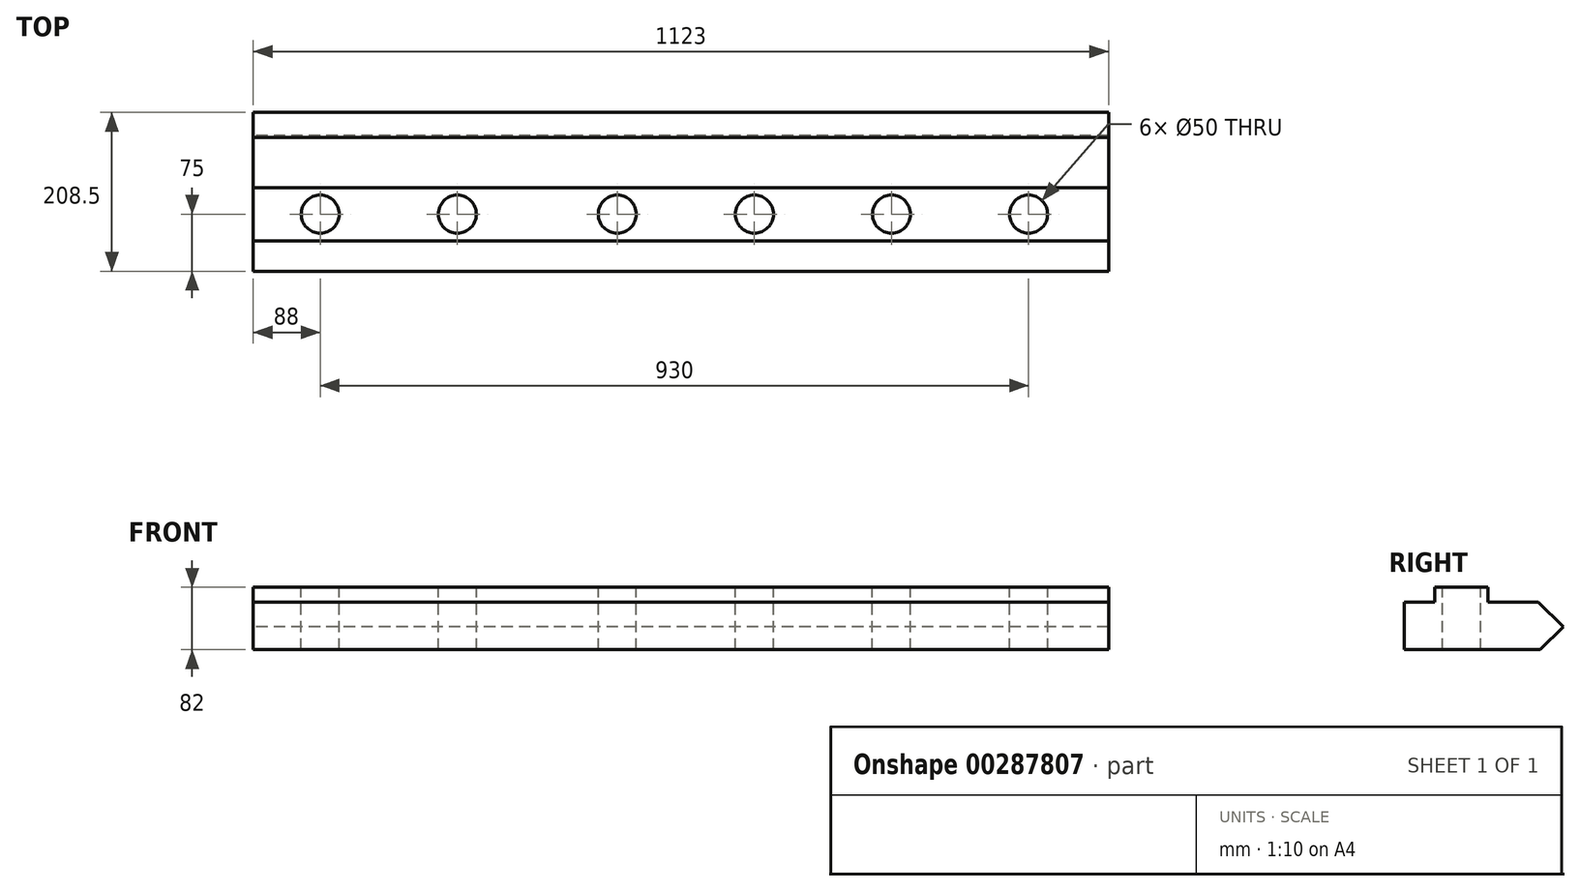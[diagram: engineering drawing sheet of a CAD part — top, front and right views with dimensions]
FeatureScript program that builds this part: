
annotation { "Feature Type Name" : "Feature", "Feature Type Description" : "" }
export const myFeature = defineFeature(function(context is Context, id is Id, definition is map)
    precondition{}
    {
        {
            var Q0;
            Q0=qCreatedBy(makeId("Right.planeOp"),FACE);
            var sketch = newSketch(context, id + "F0", { "sketchPlane" : qUnion([Q0])});
            skLineSegment(sketch, "E0.bottom", {"start": v(0, 0) * mm, "end": v(178.5, 0) * mm});
            skLineSegment(sketch, "E0.top", {"start": v(40, 82) * mm, "end": v(110, 82) * mm});
            skLineSegment(sketch, "E0.left", {"start": v(0, 0) * mm, "end": v(0, 62.5) * mm});
            skLineSegment(sketch, "E1", {"start": v(0, 62.5) * mm, "end": v(40, 62.5) * mm});
            skLineSegment(sketch, "E2", {"start": v(40, 62.5) * mm, "end": v(40, 82) * mm});
            skLineSegment(sketch, "E3", {"start": v(208.5, 30) * mm, "end": v(176, 62.5) * mm});
            skLineSegment(sketch, "E4", {"start": v(208.5, 30) * mm, "end": v(178.5, 0) * mm});
            skLineSegment(sketch, "E5", {"start": v(110, 82) * mm, "end": v(110, 62.5) * mm});
            skLineSegment(sketch, "E6", {"start": v(110, 62.5) * mm, "end": v(176, 62.5) * mm});
            skLineSegment(sketch, "E7", {"start": v(208.5, 78.56) * mm, "end": v(208.5, -44.4) * mm, "construction": true});
            skSolve(sketch);
        }
        {
            var Q0;
            Q0=makeQuery(id+"F0.imprint","IMPRINT",FACE,{"disambiguationData":[TD([[makeQuery(id+"F0.imprint","IMPRINT",EDGE,{"derivedFrom":sQuery(id+"F0.wireOp",EDGE,"E0.bottom")}),1.0]])]});
            extrude(context, id + "F1", {"entities" : qUnion([Q0]), "endBound" : BoundingType.SYMMETRIC, "depth" : 1123 * mm});
        }
        {
            var Q0;
            Q0=makeQuery(id+"F1.opExtrude","SWEPT_FACE",FACE,{"disambiguationData":[OSD([sQuery(id+"F0.wireOp",EDGE,"E0.top")])]});
            var sketch = newSketch(context, id + "F2", { "sketchPlane" : qUnion([Q0])});
            skCircle(sketch, "E8", {"center": v(456.5, 75) * mm, "radius": 25 * mm});
            skLineSegment(sketch, "E9", {"start": v(561.5, 75) * mm, "end": v(-561.5, 75) * mm, "construction": true});
            skCircle(sketch, "E10.1.0.0", {"center": v(276.5, 75) * mm, "radius": 25 * mm});
            skCircle(sketch, "E10.2.0.0", {"center": v(96.5, 75) * mm, "radius": 25 * mm});
            skCircle(sketch, "E10.3.0.0", {"center": v(-83.5, 75) * mm, "radius": 25 * mm});
            skLineSegment(sketch, "E10.direction1", {"start": v(456.5, 75) * mm, "end": v(276.5, 75) * mm, "construction": true});
            skCircle(sketch, "E11.3.0.0", {"center": v(-293.5, 75) * mm, "radius": 25 * mm});
            skCircle(sketch, "E12.3.0.0", {"center": v(-473.5, 75) * mm, "radius": 25 * mm});
            skSolve(sketch);
        }
        {
            var Q0;
            Q0=qSketchRegion(id+"F2",true);
            extrude(context, id + "F3", {"entities" : qUnion([Q0]), "operationType" : NewBodyOperationType.REMOVE, "endBound" : BoundingType.THROUGH_ALL, "oppositeDirection" : true, "depth" : 25 * mm});
        }
    });
